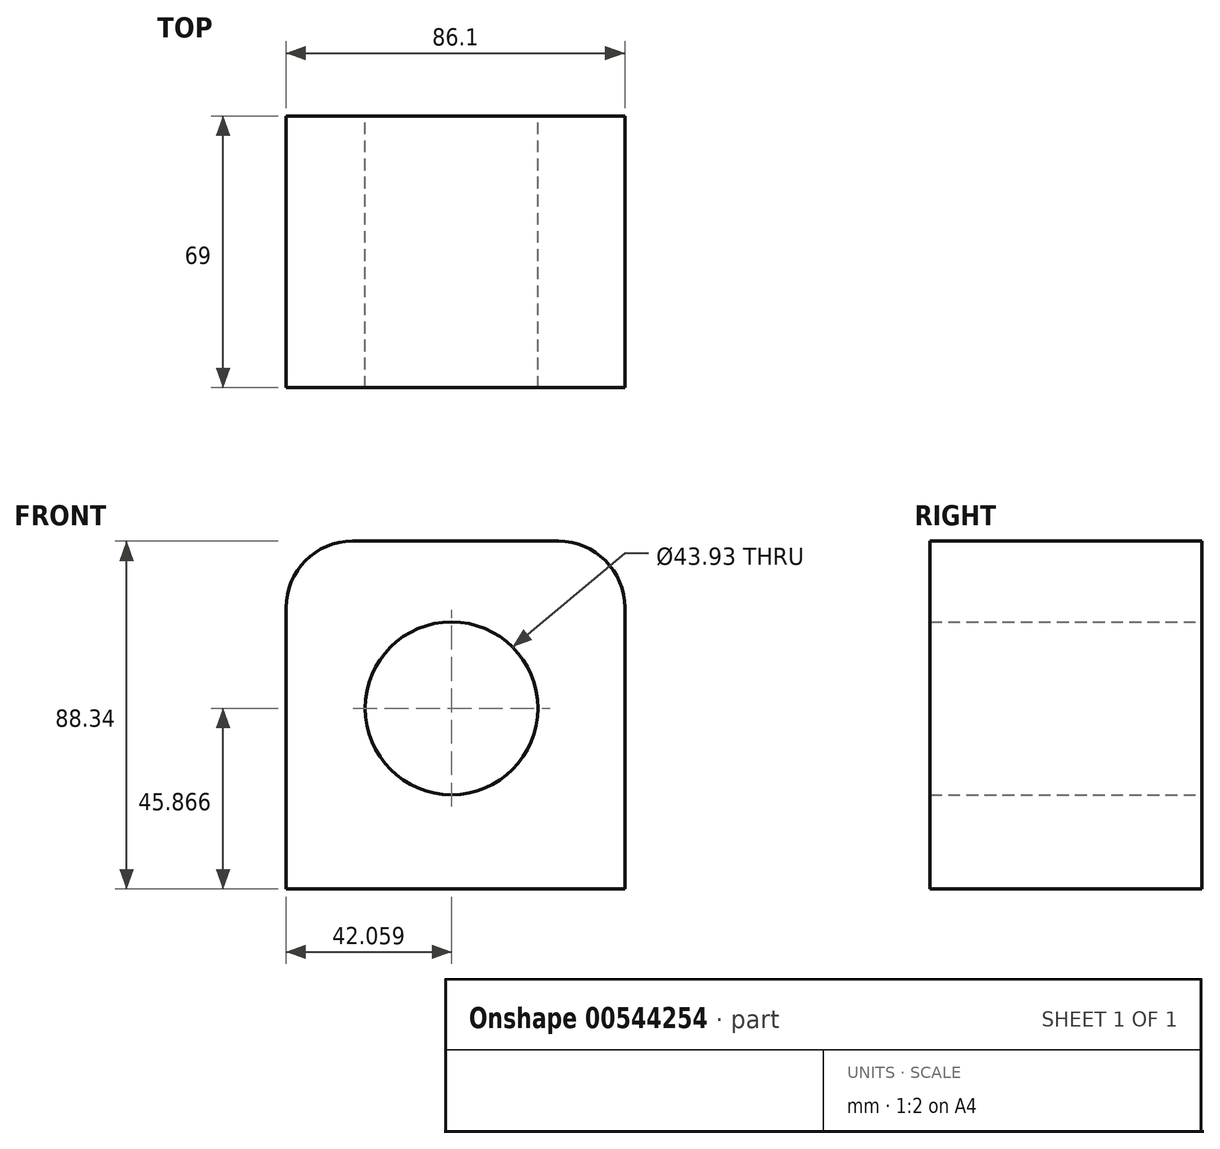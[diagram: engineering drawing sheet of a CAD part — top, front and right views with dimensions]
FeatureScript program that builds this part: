
annotation { "Feature Type Name" : "Feature", "Feature Type Description" : "" }
export const myFeature = defineFeature(function(context is Context, id is Id, definition is map)
    precondition{}
    {
        {
            var Q0;
            Q0=qCreatedBy(makeId("Front.planeOp"),FACE);
            var sketch = newSketch(context, id + "F0", { "sketchPlane" : qUnion([Q0])});
            skLineSegment(sketch, "E0.bottom", {"start": v(0, 0) * mm, "end": v(86.1, 0) * mm});
            skLineSegment(sketch, "E0.top", {"start": v(0, 88.34) * mm, "end": v(86.1, 88.34) * mm});
            skLineSegment(sketch, "E0.left", {"start": v(0, 0) * mm, "end": v(0, 88.34) * mm});
            skLineSegment(sketch, "E0.right", {"start": v(86.1, 0) * mm, "end": v(86.1, 88.34) * mm});
            skCircle(sketch, "E1", {"center": v(42.06, 45.87) * mm, "radius": 21.97 * mm});
            skSolve(sketch);
        }
        {
            var Q0;
            Q0=makeQuery(id+"F0.imprint","IMPRINT",FACE,{"disambiguationData":[TD([[makeQuery(id+"F0.imprint","IMPRINT",EDGE,{"derivedFrom":sQuery(id+"F0.wireOp",EDGE,"E0.bottom")}),1.0]])]});
            extrude(context, id + "F1", {"entities" : qUnion([Q0]), "depth" : 69 * mm, "offsetDistance" : 25 * mm});
        }
        {
            var Q0;
            Q0=makeQuery(id+"F1.opExtrude","SWEPT_EDGE",EDGE,{"disambiguationData":[OSD([sQuery(id+"F0.wireOp",EDGE,"E0.top"),sQuery(id+"F0.wireOp",EDGE,"E0.left")])]});
            var Q1;
            Q1=makeQuery(id+"F1.opExtrude","SWEPT_EDGE",EDGE,{"disambiguationData":[OSD([sQuery(id+"F0.wireOp",EDGE,"E0.top"),sQuery(id+"F0.wireOp",EDGE,"E0.right")])]});
            fillet(context, id + "F2", {"entities" : qUnion([Q0, Q1]), "radius" : 16.9 * mm, "tangentPropagation" : true, "allowEdgeOverflow" : false});
        }
    });
